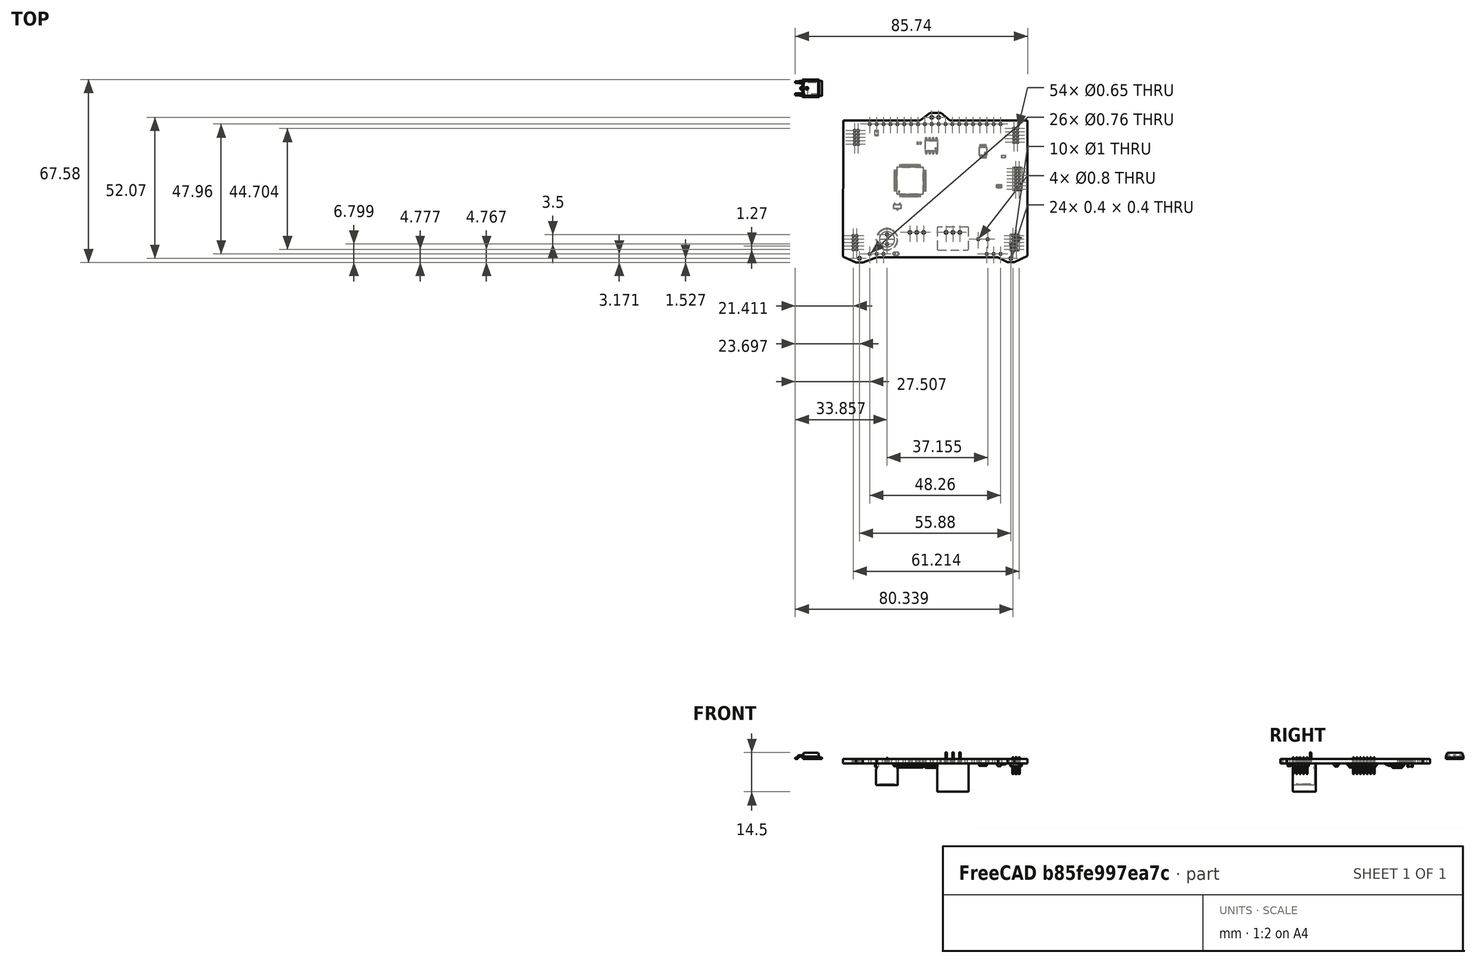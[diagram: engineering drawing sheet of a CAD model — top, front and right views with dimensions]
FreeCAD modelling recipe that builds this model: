
FCSTD DOCUMENT  (FreeCAD 1.0R39109 (Git))
Label: DICMainboard
License: All rights reserved
LicenseURL: http://en.wikipedia.org/wiki/All_rights_reserved
objects: App::Link×97, Part::Feature×24, App::Part×10, PartDesign::CoordinateSystem×1, Sketcher::SketchObject×1
note: 27 computed .brp shape members not serialized (recipe doc carries the construction recipe); baked Part::Feature solids carry a one-line shape summary decoded from their .brp

FEATURE [PartDesign::CoordinateSystem] Local_CS_e9e
  AttacherType = Attacher::AttachEngine3D
  MapMode = 2
FEATURE [Part::Feature] Pcb_e9e
  shape: bbox 68.07 x 55.25 x 1.6 mm, 110 faces (baked)
FEATURE [Sketcher::SketchObject] PCB_Sketch_e9e
  ArcFitTolerance = 1e-06
  FullyConstrained = true
  MakeInternals = false
FEATURE [Part::Feature] Shape  label="C19_C_0805_2012Metric_915db11c73f1"
  Placement = pos=(24.257,-16.448,-1.6) rot=(0.707107,0.707107,0;3.14159rad)
  shape: bbox 1.25 x 2 x 1.25 mm, 28 faces (baked)
FEATURE [Part::Feature] Shape001  label="C18_C_0603_1608Metric_10e447ca614a"
  Placement = pos=(39.878,-20.193,-1.6) rot=(1,0,0;3.14159rad)
  shape: bbox 1.6 x 0.8 x 0.8 mm, 28 faces (baked)
FEATURE [Part::Feature] Shape002  label="R42_R_0603_1608Metric_e00ced120b5b"
  Placement = pos=(70.993,-25.146,-1.6) rot=(1,0,0;3.14159rad)
  shape: bbox 1.6 x 0.8 x 0.45 mm, 26 faces (baked)
FEATURE [App::Link] R42_R_0603_1608Metric_e00ced120b5b_ln_  label="R3_R_0603_1608Metric_9b0ed8f2439a"
  LinkPlacement = pos=(35.687,-42.037,-1.6) rot=(1,0,0;3.14159rad)
  LinkedObject = -> Shape002
  Placement = pos=(35.687,-42.037,-1.6) rot=(1,0,0;3.14159rad)
FEATURE [App::Link] R42_R_0603_1608Metric_e00ced120b5b_ln_001  label="R2_R_0603_1608Metric_8df39385d074"
  LinkPlacement = pos=(27.265,-19.939,-1.6) rot=(0,1,0;3.14159rad)
  LinkedObject = -> Shape002
  Placement = pos=(27.265,-19.939,-1.6) rot=(0,1,0;3.14159rad)
FEATURE [Part::Feature] Shape003  label="C21_CP_Radial_D80mm_P350mm_b4bb79b80bd8"
  Placement = pos=(28.067,-57.531,-1.6) rot=(0.707107,0.707107,0;3.14159rad)
  shape: bbox 10.23 x 9.886 x 10 mm, 54 faces (baked)
FEATURE [App::Link] C19_C_0805_2012Metric_915db11c73f1_ln_  label="C12_C_0805_2012Metric_6993a4fefcef"
  LinkPlacement = pos=(29.972,-40.386,-1.6) rot=(0,1,0;3.14159rad)
  LinkedObject = -> Shape
  Placement = pos=(29.972,-40.386,-1.6) rot=(0,1,0;3.14159rad)
FEATURE [Part::Feature] Shape004  label="JTAG1_PinHeader_2x07_P127mm_Vertical_7ea92a9874db"
  Placement = pos=(76.835,-29.718,-1.6) rot=(0,1,0;3.14159rad)
  shape: bbox 3.4 x 8.89 x 6.3 mm, 298 faces (baked)
FEATURE [App::Link] R42_R_0603_1608Metric_e00ced120b5b_ln_002  label="R29_R_0603_1608Metric_b834401a76b2"
  LinkPlacement = pos=(60.579,-46.228,-1.6) rot=(0,1,0;3.14159rad)
  LinkedObject = -> Shape002
  Placement = pos=(60.579,-46.228,-1.6) rot=(0,1,0;3.14159rad)
FEATURE [App::Link] C18_C_0603_1608Metric_10e447ca614a_ln_  label="C29_C_0603_1608Metric_30aa2c5fb68f"
  LinkPlacement = pos=(50.546,-26.035,-1.6) rot=(1,0,0;3.14159rad)
  LinkedObject = -> Shape001
  Placement = pos=(50.546,-26.035,-1.6) rot=(1,0,0;3.14159rad)
FEATURE [App::Link] R42_R_0603_1608Metric_e00ced120b5b_ln_003  label="R36_R_0603_1608Metric_5693be527eb2"
  LinkPlacement = pos=(53.848,-26.035,-1.6) rot=(0,1,0;3.14159rad)
  LinkedObject = -> Shape002
  Placement = pos=(53.848,-26.035,-1.6) rot=(0,1,0;3.14159rad)
FEATURE [App::Link] R42_R_0603_1608Metric_e00ced120b5b_ln_004  label="R39_R_0603_1608Metric_50952633201f"
  LinkPlacement = pos=(69.215,-29.845,-1.6) rot=(0.707107,0.707107,0;3.14159rad)
  LinkedObject = -> Shape002
  Placement = pos=(69.215,-29.845,-1.6) rot=(0.707107,0.707107,0;3.14159rad)
FEATURE [Part::Feature] Shape005  label="U2_SOT_23_5143090a7d01"
  Placement = pos=(31.877,-43.688,-1.6) rot=(0.707107,-0.707107,0;3.14159rad)
  shape: bbox 3 x 2.5 x 1.2 mm, 76 faces (baked)
FEATURE [App::Link] U2_SOT_23_5143090a7d01_ln_  label="Q2_SOT_23_a46526c7cbaa"
  LinkPlacement = pos=(65.786,-38.735,-1.6) rot=(0.707107,0.707107,0;3.14159rad)
  LinkedObject = -> Shape005
  Placement = pos=(65.786,-38.735,-1.6) rot=(0.707107,0.707107,0;3.14159rad)
FEATURE [App::Link] R42_R_0603_1608Metric_e00ced120b5b_ln_005  label="R31_R_0603_1608Metric_b000aee3d83a"
  LinkPlacement = pos=(59.309,-28.702,-1.6) rot=(0,1,0;3.14159rad)
  LinkedObject = -> Shape002
  Placement = pos=(59.309,-28.702,-1.6) rot=(0,1,0;3.14159rad)
FEATURE [App::Link] C18_C_0603_1608Metric_10e447ca614a_ln_001  label="C5_C_0603_1608Metric_679d8c6e1927"
  LinkPlacement = pos=(34.417,-44.45,-1.6) rot=(0.707107,0.707107,0;3.14159rad)
  LinkedObject = -> Shape001
  Placement = pos=(34.417,-44.45,-1.6) rot=(0.707107,0.707107,0;3.14159rad)
FEATURE [App::Link] C18_C_0603_1608Metric_10e447ca614a_ln_002  label="C6_C_0603_1608Metric_e41e872100cf"
  LinkPlacement = pos=(39.116,-24.322,-1.6) rot=(0,1,0;3.14159rad)
  LinkedObject = -> Shape001
  Placement = pos=(39.116,-24.322,-1.6) rot=(0,1,0;3.14159rad)
FEATURE [Part::Feature] Shape006  label="12VGood1_LED_0805_2012Metric_2ad75f4ca093"
  Placement = pos=(69.469,-36.195,-1.6) rot=(0,1,0;3.14159rad)
  shape: bbox 2 x 1.25 x 1.1 mm, 50 faces (baked)
FEATURE [App::Link] C19_C_0805_2012Metric_915db11c73f1_ln_001  label="C14_C_0805_2012Metric_060f63ed2ef4"
  LinkPlacement = pos=(42.418,-49.911,-1.6) rot=(1,0,0;3.14159rad)
  LinkedObject = -> Shape
  Placement = pos=(42.418,-49.911,-1.6) rot=(1,0,0;3.14159rad)
FEATURE [App::Link] R42_R_0603_1608Metric_e00ced120b5b_ln_006  label="R30_R_0603_1608Metric_8c3fd63a3134"
  LinkPlacement = pos=(50.8,-42.926,-1.6) rot=(0,1,0;3.14159rad)
  LinkedObject = -> Shape002
  Placement = pos=(50.8,-42.926,-1.6) rot=(0,1,0;3.14159rad)
FEATURE [App::Link] C18_C_0603_1608Metric_10e447ca614a_ln_003  label="C17_C_0603_1608Metric_5bd1929c3623"
  LinkPlacement = pos=(39.878,-21.971,-1.6) rot=(1,0,0;3.14159rad)
  LinkedObject = -> Shape001
  Placement = pos=(39.878,-21.971,-1.6) rot=(1,0,0;3.14159rad)
FEATURE [App::Link] R42_R_0603_1608Metric_e00ced120b5b_ln_007  label="R25_R_0603_1608Metric_14260ea3fd4e"
  LinkPlacement = pos=(64.77,-44.704,-1.6) rot=(0,1,0;3.14159rad)
  LinkedObject = -> Shape002
  Placement = pos=(64.77,-44.704,-1.6) rot=(0,1,0;3.14159rad)
FEATURE [Part::Feature] Shape007  label="U10_MSOP_8_3x3mm_P065mm_82bb67e16242"
  Placement = pos=(63.5,-23.241,-1.6) rot=(0.707107,0.707107,0;3.14159rad)
  shape: bbox 3 x 4.9 x 0.95 mm, 156 faces (baked)
FEATURE [App::Link] U2_SOT_23_5143090a7d01_ln_001  label="Q1_SOT_23_1223d9ad7d7e"
  LinkPlacement = pos=(68.072,-33.274,-1.6) rot=(1,0,0;3.14159rad)
  LinkedObject = -> Shape005
  Placement = pos=(68.072,-33.274,-1.6) rot=(1,0,0;3.14159rad)
FEATURE [App::Link] C19_C_0805_2012Metric_915db11c73f1_ln_002  label="C11_C_0805_2012Metric_20aa78c893d6"
  LinkPlacement = pos=(54.2075,-49.53,-1.6) rot=(0,1,0;3.14159rad)
  LinkedObject = -> Shape
  Placement = pos=(54.2075,-49.53,-1.6) rot=(0,1,0;3.14159rad)
FEATURE [Part::Feature] Shape008  label="J3_PinHeader_2x05_P127mm_Vertical_4a0e541a8516"
  Placement = pos=(75.819,-54.473,-1.6) rot=(0,1,0;3.14159rad)
  shape: bbox 3.4 x 6.35 x 6.3 mm, 214 faces (baked)
FEATURE [App::Link] R42_R_0603_1608Metric_e00ced120b5b_ln_008  label="R1_R_0603_1608Metric_52185c8e4965"
  LinkPlacement = pos=(27.265,-22.733,-1.6) rot=(1,0,0;3.14159rad)
  LinkedObject = -> Shape002
  Placement = pos=(27.265,-22.733,-1.6) rot=(1,0,0;3.14159rad)
FEATURE [App::Link] C19_C_0805_2012Metric_915db11c73f1_ln_003  label="C7_C_0805_2012Metric_b3b50e9b0364"
  LinkPlacement = pos=(50.2705,-49.53,-1.6) rot=(1,0,0;3.14159rad)
  LinkedObject = -> Shape
  Placement = pos=(50.2705,-49.53,-1.6) rot=(1,0,0;3.14159rad)
FEATURE [App::Link] U10_MSOP_8_3x3mm_P065mm_82bb67e16242_ln_  label="U9_MSOP_8_3x3mm_P065mm_9b50181ec5fb"
  LinkPlacement = pos=(57.023,-41.91,-1.6) rot=(1,0,0;3.14159rad)
  LinkedObject = -> Shape007
  Placement = pos=(57.023,-41.91,-1.6) rot=(1,0,0;3.14159rad)
FEATURE [App::Link] _2VGood1_LED_0805_2012Metric_2ad75f4ca093_ln_  label="5VGood1_LED_0805_2012Metric_60cda601a8c1"
  LinkPlacement = pos=(51.943,-60.96,-1.6) rot=(0,1,0;3.14159rad)
  LinkedObject = -> Shape006
  Placement = pos=(51.943,-60.96,-1.6) rot=(0,1,0;3.14159rad)
FEATURE [App::Link] U2_SOT_23_5143090a7d01_ln_002  label="Q3_SOT_23_1241f12d323f"
  LinkPlacement = pos=(59.055,-32.766,-1.6) rot=(1,0,0;3.14159rad)
  LinkedObject = -> Shape005
  Placement = pos=(59.055,-32.766,-1.6) rot=(1,0,0;3.14159rad)
FEATURE [App::Link] C18_C_0603_1608Metric_10e447ca614a_ln_004  label="C2_C_0603_1608Metric_784de1c4b5be"
  LinkPlacement = pos=(27.178,-37.28,-1.6) rot=(0.707107,0.707107,0;3.14159rad)
  LinkedObject = -> Shape001
  Placement = pos=(27.178,-37.28,-1.6) rot=(0.707107,0.707107,0;3.14159rad)
FEATURE [Part::Feature] Shape009  label="D10_D_SOD_323_1cf1e5386782"
  Placement = pos=(31.369,-61.087,-1.6) rot=(1,0,0;3.14159rad)
  shape: bbox 2.5 x 1.25 x 1.1 mm, 67 faces (baked)
FEATURE [App::Link] D10_D_SOD_323_1cf1e5386782_ln_  label="D8_D_SOD_323_442fc4d99dd7"
  LinkPlacement = pos=(52.324,-24.257,-1.6) rot=(1,0,0;3.14159rad)
  LinkedObject = -> Shape009
  Placement = pos=(52.324,-24.257,-1.6) rot=(1,0,0;3.14159rad)
FEATURE [App::Link] R42_R_0603_1608Metric_e00ced120b5b_ln_009  label="R46_R_0603_1608Metric_d391e1cc1bf8"
  LinkPlacement = pos=(55.88,-18.923,-1.6) rot=(1,0,0;3.14159rad)
  LinkedObject = -> Shape002
  Placement = pos=(55.88,-18.923,-1.6) rot=(1,0,0;3.14159rad)
FEATURE [App::Link] R42_R_0603_1608Metric_e00ced120b5b_ln_010  label="R44_R_0603_1608Metric_76086e2af044"
  LinkPlacement = pos=(70.993,-21.59,-1.6) rot=(0,1,0;3.14159rad)
  LinkedObject = -> Shape002
  Placement = pos=(70.993,-21.59,-1.6) rot=(0,1,0;3.14159rad)
FEATURE [App::Link] R42_R_0603_1608Metric_e00ced120b5b_ln_011  label="R24_R_0603_1608Metric_616434719463"
  LinkPlacement = pos=(62.357,-43.815,-1.6) rot=(0.707107,-0.707107,0;3.14159rad)
  LinkedObject = -> Shape002
  Placement = pos=(62.357,-43.815,-1.6) rot=(0.707107,-0.707107,0;3.14159rad)
FEATURE [App::Link] U2_SOT_23_5143090a7d01_ln_003  label="Q6_SOT_23_f7e973546728"
  LinkPlacement = pos=(67.31,-23.876,-1.6) rot=(1,0,0;3.14159rad)
  LinkedObject = -> Shape005
  Placement = pos=(67.31,-23.876,-1.6) rot=(1,0,0;3.14159rad)
FEATURE [App::Link] C18_C_0603_1608Metric_10e447ca614a_ln_005  label="C31_C_0603_1608Metric_179902ffe984"
  LinkPlacement = pos=(58.801,-24.638,-1.6) rot=(1,0,0;3.14159rad)
  LinkedObject = -> Shape001
  Placement = pos=(58.801,-24.638,-1.6) rot=(1,0,0;3.14159rad)
FEATURE [App::Link] C18_C_0603_1608Metric_10e447ca614a_ln_006  label="C25_C_0603_1608Metric_a51b3fc9b87c"
  LinkPlacement = pos=(48.26,-46.101,-1.6) rot=(1,0,0;3.14159rad)
  LinkedObject = -> Shape001
  Placement = pos=(48.26,-46.101,-1.6) rot=(1,0,0;3.14159rad)
FEATURE [App::Link] J3_PinHeader_2x05_P127mm_Vertical_4a0e541a8516_ln_  label="J5_PinHeader_2x05_P127mm_Vertical_21cfdfc90ae7"
  LinkPlacement = pos=(16.891,-54.483,-1.6) rot=(0,1,0;3.14159rad)
  LinkedObject = -> Shape008
  Placement = pos=(16.891,-54.483,-1.6) rot=(0,1,0;3.14159rad)
FEATURE [App::Link] D10_D_SOD_323_1cf1e5386782_ln_001  label="D2_D_SOD_323_81fae5dc7b6e"
  LinkPlacement = pos=(47.371,-48.895,-1.6) rot=(0.707107,0.707107,0;3.14159rad)
  LinkedObject = -> Shape009
  Placement = pos=(47.371,-48.895,-1.6) rot=(0.707107,0.707107,0;3.14159rad)
FEATURE [App::Link] R42_R_0603_1608Metric_e00ced120b5b_ln_012  label="R28_R_0603_1608Metric_524fb33c0c76"
  LinkPlacement = pos=(59.7385,-49.596,-1.6) rot=(0.707107,0.707107,0;3.14159rad)
  LinkedObject = -> Shape002
  Placement = pos=(59.7385,-49.596,-1.6) rot=(0.707107,0.707107,0;3.14159rad)
FEATURE [App::Link] R42_R_0603_1608Metric_e00ced120b5b_ln_013  label="R9_R_0603_1608Metric_39820daff148"
  LinkPlacement = pos=(31.877,-18.607,-1.6) rot=(0.707107,0.707107,0;3.14159rad)
  LinkedObject = -> Shape002
  Placement = pos=(31.877,-18.607,-1.6) rot=(0.707107,0.707107,0;3.14159rad)
FEATURE [App::Link] C18_C_0603_1608Metric_10e447ca614a_ln_007  label="C28_C_0603_1608Metric_9930d46ac3f8"
  LinkPlacement = pos=(53.467,-18.288,-1.6) rot=(0.707107,0.707107,0;3.14159rad)
  LinkedObject = -> Shape001
  Placement = pos=(53.467,-18.288,-1.6) rot=(0.707107,0.707107,0;3.14159rad)
FEATURE [App::Link] R42_R_0603_1608Metric_e00ced120b5b_ln_014  label="R23_R_0603_1608Metric_14708d2771e9"
  LinkPlacement = pos=(68.199,-51.308,-1.6) rot=(0.707107,-0.707107,0;3.14159rad)
  LinkedObject = -> Shape002
  Placement = pos=(68.199,-51.308,-1.6) rot=(0.707107,-0.707107,0;3.14159rad)
FEATURE [App::Link] C19_C_0805_2012Metric_915db11c73f1_ln_004  label="C23_C_0805_2012Metric_29fb196ac7a2"
  LinkPlacement = pos=(70.231,-40.386,-1.6) rot=(0,1,0;3.14159rad)
  LinkedObject = -> Shape
  Placement = pos=(70.231,-40.386,-1.6) rot=(0,1,0;3.14159rad)
FEATURE [Part::Feature] Shape010  label="U1_Converter_DCDC_RECOM_R_78E_05_THT_7495ffbcc0e0"
  Placement = pos=(49.877,-53.213,-1.6) rot=(1,0,0;3.14159rad)
  shape: bbox 11.67 x 8.57 x 14.5 mm, 27 faces (baked)
FEATURE [App::Link] _2VGood1_LED_0805_2012Metric_2ad75f4ca093_ln_001  label="Error1_LED_0805_2012Metric_0193bb44fb5e"
  LinkPlacement = pos=(23.455,-19.939,-1.6) rot=(0,1,0;3.14159rad)
  LinkedObject = -> Shape006
  Placement = pos=(23.455,-19.939,-1.6) rot=(0,1,0;3.14159rad)
FEATURE [App::Link] C19_C_0805_2012Metric_915db11c73f1_ln_005  label="C15_C_0805_2012Metric_c2950c4f82bb"
  LinkPlacement = pos=(45.339,-49.022,-1.6) rot=(0.707107,0.707107,0;3.14159rad)
  LinkedObject = -> Shape
  Placement = pos=(45.339,-49.022,-1.6) rot=(0.707107,0.707107,0;3.14159rad)
FEATURE [App::Link] R42_R_0603_1608Metric_e00ced120b5b_ln_015  label="R11_R_0603_1608Metric_fc6ec5a46fb0"
  LinkPlacement = pos=(44.45,-16.699,-1.6) rot=(1,0,0;3.14159rad)
  LinkedObject = -> Shape002
  Placement = pos=(44.45,-16.699,-1.6) rot=(1,0,0;3.14159rad)
FEATURE [App::Link] R42_R_0603_1608Metric_e00ced120b5b_ln_016  label="R43_R_0603_1608Metric_bffcf2708168"
  LinkPlacement = pos=(65.786,-17.907,-1.6) rot=(0,1,0;3.14159rad)
  LinkedObject = -> Shape002
  Placement = pos=(65.786,-17.907,-1.6) rot=(0,1,0;3.14159rad)
FEATURE [App::Link] D10_D_SOD_323_1cf1e5386782_ln_002  label="D3_D_SOD_323_b8dc3af82ad9"
  LinkPlacement = pos=(58.674,-22.225,-1.6) rot=(1,0,0;3.14159rad)
  LinkedObject = -> Shape009
  Placement = pos=(58.674,-22.225,-1.6) rot=(1,0,0;3.14159rad)
FEATURE [App::Link] R42_R_0603_1608Metric_e00ced120b5b_ln_017  label="R38_R_0603_1608Metric_037dd372ccbc"
  LinkPlacement = pos=(70.739,-27.686,-1.6) rot=(0.707107,0.707107,0;3.14159rad)
  LinkedObject = -> Shape002
  Placement = pos=(70.739,-27.686,-1.6) rot=(0.707107,0.707107,0;3.14159rad)
FEATURE [App::Link] C19_C_0805_2012Metric_915db11c73f1_ln_006  label="C20_C_0805_2012Metric_feb99ca7776e"
  LinkPlacement = pos=(31.877,-15.686,-1.6) rot=(0,1,0;3.14159rad)
  LinkedObject = -> Shape
  Placement = pos=(31.877,-15.686,-1.6) rot=(0,1,0;3.14159rad)
FEATURE [App::Link] R42_R_0603_1608Metric_e00ced120b5b_ln_018  label="R37_R_0603_1608Metric_1e3016d2806e"
  LinkPlacement = pos=(70.993,-23.241,-1.6) rot=(0,1,0;3.14159rad)
  LinkedObject = -> Shape002
  Placement = pos=(70.993,-23.241,-1.6) rot=(0,1,0;3.14159rad)
FEATURE [Part::Feature] Shape011  label="U7_SOIC_8_39x49mm_P127mm_1499a48e6e93"
  Placement = pos=(44.45,-21.209,-1.6) rot=(0.707107,0.707107,0;3.14159rad)
  shape: bbox 4.9 x 6 x 1.75 mm, 156 faces (baked)
FEATURE [App::Link] R42_R_0603_1608Metric_e00ced120b5b_ln_019  label="R10_R_0603_1608Metric_863b16e2652c"
  LinkPlacement = pos=(48.133,-19.558,-1.6) rot=(0.707107,0.707107,0;3.14159rad)
  LinkedObject = -> Shape002
  Placement = pos=(48.133,-19.558,-1.6) rot=(0.707107,0.707107,0;3.14159rad)
FEATURE [App::Link] R42_R_0603_1608Metric_e00ced120b5b_ln_020  label="R7_R_0603_1608Metric_1723f24f5f2f"
  LinkPlacement = pos=(78.105,-43.688,-1.6) rot=(0.707107,0.707107,0;3.14159rad)
  LinkedObject = -> Shape002
  Placement = pos=(78.105,-43.688,-1.6) rot=(0.707107,0.707107,0;3.14159rad)
FEATURE [App::Link] C18_C_0603_1608Metric_10e447ca614a_ln_008  label="C4_C_0603_1608Metric_5f5500ef63df"
  LinkPlacement = pos=(32.131,-25.146,-1.6) rot=(0,1,0;3.14159rad)
  LinkedObject = -> Shape001
  Placement = pos=(32.131,-25.146,-1.6) rot=(0,1,0;3.14159rad)
FEATURE [App::Link] R42_R_0603_1608Metric_e00ced120b5b_ln_021  label="R17_R_0603_1608Metric_fc738fbfad18"
  LinkPlacement = pos=(70.739,-30.988,-1.6) rot=(0.707107,0.707107,0;3.14159rad)
  LinkedObject = -> Shape002
  Placement = pos=(70.739,-30.988,-1.6) rot=(0.707107,0.707107,0;3.14159rad)
FEATURE [App::Link] U2_SOT_23_5143090a7d01_ln_004  label="Q7_SOT_23_bc60db84acee"
  LinkPlacement = pos=(63.627,-29.845,-1.6) rot=(1,0,0;3.14159rad)
  LinkedObject = -> Shape005
  Placement = pos=(63.627,-29.845,-1.6) rot=(1,0,0;3.14159rad)
FEATURE [App::Link] U1_Converter_DCDC_RECOM_R_78E_05_THT_7495ffbcc0e0_ln_  label="U5_Converter_DCDC_RECOM_R_78E_05_THT_6eb4cbfbcd04"
  LinkPlacement = pos=(36.542,-53.213,-1.6) rot=(1,0,0;3.14159rad)
  LinkedObject = -> Shape010
  Placement = pos=(36.542,-53.213,-1.6) rot=(1,0,0;3.14159rad)
FEATURE [App::Link] R42_R_0603_1608Metric_e00ced120b5b_ln_022  label="R26_R_0603_1608Metric_34ca61038909"
  LinkPlacement = pos=(67.691,-28.829,-1.6) rot=(0.707107,-0.707107,0;3.14159rad)
  LinkedObject = -> Shape002
  Placement = pos=(67.691,-28.829,-1.6) rot=(0.707107,-0.707107,0;3.14159rad)
FEATURE [App::Link] R42_R_0603_1608Metric_e00ced120b5b_ln_023  label="R27_R_0603_1608Metric_60e756865c77"
  LinkPlacement = pos=(67.183,-43.815,-1.6) rot=(0.707107,0.707107,0;3.14159rad)
  LinkedObject = -> Shape002
  Placement = pos=(67.183,-43.815,-1.6) rot=(0.707107,0.707107,0;3.14159rad)
FEATURE [App::Link] R42_R_0603_1608Metric_e00ced120b5b_ln_024  label="R14_R_0603_1608Metric_d767aa6e1c7e"
  LinkPlacement = pos=(58.928,-37.592,-1.6) rot=(0,1,0;3.14159rad)
  LinkedObject = -> Shape002
  Placement = pos=(58.928,-37.592,-1.6) rot=(0,1,0;3.14159rad)
FEATURE [App::Link] R42_R_0603_1608Metric_e00ced120b5b_ln_025  label="R35_R_0603_1608Metric_a89be60451e6"
  LinkPlacement = pos=(67.056,-26.416,-1.6) rot=(0,1,0;3.14159rad)
  LinkedObject = -> Shape002
  Placement = pos=(67.056,-26.416,-1.6) rot=(0,1,0;3.14159rad)
FEATURE [App::Link] R42_R_0603_1608Metric_e00ced120b5b_ln_026  label="R12_R_0603_1608Metric_98ba704dd8f1"
  LinkPlacement = pos=(65.786,-41.402,-1.6) rot=(0,1,0;3.14159rad)
  LinkedObject = -> Shape002
  Placement = pos=(65.786,-41.402,-1.6) rot=(0,1,0;3.14159rad)
FEATURE [App::Link] C18_C_0603_1608Metric_10e447ca614a_ln_009  label="C1_C_0603_1608Metric_84c5a7f979f1"
  LinkPlacement = pos=(32.131,-23.495,-1.6) rot=(0,1,0;3.14159rad)
  LinkedObject = -> Shape001
  Placement = pos=(32.131,-23.495,-1.6) rot=(0,1,0;3.14159rad)
FEATURE [App::Link] U2_SOT_23_5143090a7d01_ln_005  label="Q5_SOT_23_2fb3d1e9febb"
  LinkPlacement = pos=(62.9135,-49.596,-1.6) rot=(1,0,0;3.14159rad)
  LinkedObject = -> Shape005
  Placement = pos=(62.9135,-49.596,-1.6) rot=(1,0,0;3.14159rad)
FEATURE [App::Link] _2VGood1_LED_0805_2012Metric_2ad75f4ca093_ln_002  label="Heart1_LED_0805_2012Metric_c9bdaa238e08"
  LinkPlacement = pos=(23.455,-22.733,-1.6) rot=(0,1,0;3.14159rad)
  LinkedObject = -> Shape006
  Placement = pos=(23.455,-22.733,-1.6) rot=(0,1,0;3.14159rad)
FEATURE [App::Link] C18_C_0603_1608Metric_10e447ca614a_ln_010  label="C8_C_0603_1608Metric_bdc2e3e24877"
  LinkPlacement = pos=(39.116,-25.973,-1.6) rot=(0,1,0;3.14159rad)
  LinkedObject = -> Shape001
  Placement = pos=(39.116,-25.973,-1.6) rot=(0,1,0;3.14159rad)
FEATURE [App::Link] C19_C_0805_2012Metric_915db11c73f1_ln_007  label="C22_C_0805_2012Metric_28f6afd9b51f"
  LinkPlacement = pos=(69.977,-54.61,-1.6) rot=(0,1,0;3.14159rad)
  LinkedObject = -> Shape
  Placement = pos=(69.977,-54.61,-1.6) rot=(0,1,0;3.14159rad)
FEATURE [App::Link] C18_C_0603_1608Metric_10e447ca614a_ln_011  label="C3_C_0603_1608Metric_22f7aa9a1690"
  LinkPlacement = pos=(27.178,-33.782,-1.6) rot=(0.707107,-0.707107,0;3.14159rad)
  LinkedObject = -> Shape001
  Placement = pos=(27.178,-33.782,-1.6) rot=(0.707107,-0.707107,0;3.14159rad)
FEATURE [App::Link] R42_R_0603_1608Metric_e00ced120b5b_ln_027  label="R20_R_0603_1608Metric_2b4dd9f72b59"
  LinkPlacement = pos=(57.404,-39.116,-1.6) rot=(1,0,0;3.14159rad)
  LinkedObject = -> Shape002
  Placement = pos=(57.404,-39.116,-1.6) rot=(1,0,0;3.14159rad)
FEATURE [App::Link] R42_R_0603_1608Metric_e00ced120b5b_ln_028  label="R8_R_0603_1608Metric_7230250cfa97"
  LinkPlacement = pos=(69.596,-38.354,-1.6) rot=(1,0,0;3.14159rad)
  LinkedObject = -> Shape002
  Placement = pos=(69.596,-38.354,-1.6) rot=(1,0,0;3.14159rad)
FEATURE [App::Link] R42_R_0603_1608Metric_e00ced120b5b_ln_029  label="R6_R_0603_1608Metric_956f91f139f8"
  LinkPlacement = pos=(43.434,-60.96,-1.6) rot=(1,0,0;3.14159rad)
  LinkedObject = -> Shape002
  Placement = pos=(43.434,-60.96,-1.6) rot=(1,0,0;3.14159rad)
FEATURE [App::Link] R42_R_0603_1608Metric_e00ced120b5b_ln_030  label="R15_R_0603_1608Metric_29f9765fedca"
  LinkPlacement = pos=(57.15,-36.068,-1.6) rot=(0,1,0;3.14159rad)
  LinkedObject = -> Shape002
  Placement = pos=(57.15,-36.068,-1.6) rot=(0,1,0;3.14159rad)
FEATURE [App::Link] _2VGood1_LED_0805_2012Metric_2ad75f4ca093_ln_003  label="3V3Good1_LED_0805_2012Metric_f770177cd55f"
  LinkPlacement = pos=(39.624,-60.96,-1.6) rot=(1,0,0;3.14159rad)
  LinkedObject = -> Shape006
  Placement = pos=(39.624,-60.96,-1.6) rot=(1,0,0;3.14159rad)
FEATURE [App::Link] R42_R_0603_1608Metric_e00ced120b5b_ln_031  label="R13_R_0603_1608Metric_88249867bc70"
  LinkPlacement = pos=(64.389,-33.528,-1.6) rot=(0,1,0;3.14159rad)
  LinkedObject = -> Shape002
  Placement = pos=(64.389,-33.528,-1.6) rot=(0,1,0;3.14159rad)
FEATURE [App::Link] R42_R_0603_1608Metric_e00ced120b5b_ln_032  label="R18_R_0603_1608Metric_e7deeba773bd"
  LinkPlacement = pos=(54.991,-33.655,-1.6) rot=(0,1,0;3.14159rad)
  LinkedObject = -> Shape002
  Placement = pos=(54.991,-33.655,-1.6) rot=(0,1,0;3.14159rad)
FEATURE [App::Link] R42_R_0603_1608Metric_e00ced120b5b_ln_033  label="R41_R_0603_1608Metric_2dfa8f3c3e90"
  LinkPlacement = pos=(59.436,-18.796,-1.6) rot=(0.707107,-0.707107,0;3.14159rad)
  LinkedObject = -> Shape002
  Placement = pos=(59.436,-18.796,-1.6) rot=(0.707107,-0.707107,0;3.14159rad)
FEATURE [App::Link] C18_C_0603_1608Metric_10e447ca614a_ln_012  label="C30_C_0603_1608Metric_0742e3473aaa"
  LinkPlacement = pos=(50.8,-41.402,-1.6) rot=(0,1,0;3.14159rad)
  LinkedObject = -> Shape001
  Placement = pos=(50.8,-41.402,-1.6) rot=(0,1,0;3.14159rad)
FEATURE [App::Link] R42_R_0603_1608Metric_e00ced120b5b_ln_034  label="R21_R_0603_1608Metric_9688ea295803"
  LinkPlacement = pos=(51.308,-36.957,-1.6) rot=(1,0,0;3.14159rad)
  LinkedObject = -> Shape002
  Placement = pos=(51.308,-36.957,-1.6) rot=(1,0,0;3.14159rad)
FEATURE [App::Link] J3_PinHeader_2x05_P127mm_Vertical_4a0e541a8516_ln_001  label="J4_PinHeader_2x05_P127mm_Vertical_89510c161731"
  LinkPlacement = pos=(16.129,-20.701,-1.6) rot=(1,0,0;3.14159rad)
  LinkedObject = -> Shape008
  Placement = pos=(16.129,-20.701,-1.6) rot=(1,0,0;3.14159rad)
FEATURE [Part::Feature] Part__Feature  label="932d09b3-9c39-11ed-93f0-dde97e994e83_part"
  shape: bbox 6.22 x 6.5 x 2.3 mm, 13 faces (baked)
FEATURE [App::Part] _32d09b3_9c39_11ed_93f0_dde97e994e83  label="932d09b3-9c39-11ed-93f0-dde97e994e83"
  Group = -> [Part__Feature]
  Origin = -> Origin008
FEATURE [Part::Feature] Part__Feature001  label="932d09b4-9c39-11ed-93f0-dde97e994e83_part"
  shape: bbox 5.24 x 5.4 x 0.5 mm, 16 faces (baked)
FEATURE [App::Part] _32d09b4_9c39_11ed_93f0_dde97e994e83  label="932d09b4-9c39-11ed-93f0-dde97e994e83"
  Group = -> [Part__Feature001]
  Origin = -> Origin009
FEATURE [Part::Feature] Part__Feature002  label="932d09b5-9c39-11ed-93f0-dde97e994e83_part"
  shape: bbox 3.552 x 0.99 x 1.44 mm, 22 faces (baked)
FEATURE [Part::Feature] Part__Feature003  label="932d09b5-9c39-11ed-93f0-dde97e994e83_part001"
  shape: bbox 1.672 x 0.99 x 0.5 mm, 10 faces (baked)
FEATURE [Part::Feature] Part__Feature004  label="932d09b5-9c39-11ed-93f0-dde97e994e83_part002"
  shape: bbox 3.552 x 0.99 x 1.44 mm, 22 faces (baked)
FEATURE [App::Part] _32d09b5_9c39_11ed_93f0_dde97e994e83_part  label="932d09b5-9c39-11ed-93f0-dde97e994e83_part003"
  Group = -> [Part__Feature002,Part__Feature003,Part__Feature004]
  Origin = -> Origin010
FEATURE [App::Part] _32d09b5_9c39_11ed_93f0_dde97e994e83  label="932d09b5-9c39-11ed-93f0-dde97e994e83"
  Group = -> [_32d09b5_9c39_11ed_93f0_dde97e994e83_part]
  Origin = -> Origin011
FEATURE [App::Part] _32d09b2_9c39_11ed_93f0_dde97e994e83  label="932d09b2-9c39-11ed-93f0-dde97e994e83"
  Group = -> [_32d09b3_9c39_11ed_93f0_dde97e994e83,_32d09b4_9c39_11ed_93f0_dde97e994e83,_32d09b5_9c39_11ed_93f0_dde97e994e83]
  Origin = -> Origin012
FEATURE [App::Part] CQ_assembly  label="U8_CQ assembly_9e30a5f4f37c"
  Group = -> [_32d09b2_9c39_11ed_93f0_dde97e994e83]
  Origin = -> Origin013
  Placement = pos=(73.025,-46.472,-1.6) rot=(0.707107,0.707107,0;3.14159rad)
FEATURE [App::Link] C19_C_0805_2012Metric_915db11c73f1_ln_008  label="C26_C_0805_2012Metric_58a7a7612ec2"
  LinkPlacement = pos=(57.15,-47.244,-1.6) rot=(0.707107,-0.707107,0;3.14159rad)
  LinkedObject = -> Shape
  Placement = pos=(57.15,-47.244,-1.6) rot=(0.707107,-0.707107,0;3.14159rad)
FEATURE [App::Link] R42_R_0603_1608Metric_e00ced120b5b_ln_035  label="R19_R_0603_1608Metric_4285ec9b66e1"
  LinkPlacement = pos=(54.483,-36.957,-1.6) rot=(0.707107,-0.707107,0;3.14159rad)
  LinkedObject = -> Shape002
  Placement = pos=(54.483,-36.957,-1.6) rot=(0.707107,-0.707107,0;3.14159rad)
FEATURE [App::Link] U2_SOT_23_5143090a7d01_ln_006  label="Q8_SOT_23_4a5958cf5442"
  LinkPlacement = pos=(69.85,-17.526,-1.6) rot=(1,0,0;3.14159rad)
  LinkedObject = -> Shape005
  Placement = pos=(69.85,-17.526,-1.6) rot=(1,0,0;3.14159rad)
FEATURE [App::Link] R42_R_0603_1608Metric_e00ced120b5b_ln_036  label="R33_R_0603_1608Metric_c9c509e34e71"
  LinkPlacement = pos=(49.149,-44.577,-1.6) rot=(0,1,0;3.14159rad)
  LinkedObject = -> Shape002
  Placement = pos=(49.149,-44.577,-1.6) rot=(0,1,0;3.14159rad)
FEATURE [App::Link] R42_R_0603_1608Metric_e00ced120b5b_ln_037  label="R34_R_0603_1608Metric_85fe14c106d9"
  LinkPlacement = pos=(53.848,-27.686,-1.6) rot=(1,0,0;3.14159rad)
  LinkedObject = -> Shape002
  Placement = pos=(53.848,-27.686,-1.6) rot=(1,0,0;3.14159rad)
FEATURE [App::Link] R42_R_0603_1608Metric_e00ced120b5b_ln_038  label="R16_R_0603_1608Metric_68531f109549"
  LinkPlacement = pos=(62.357,-37.592,-1.6) rot=(0,1,0;3.14159rad)
  LinkedObject = -> Shape002
  Placement = pos=(62.357,-37.592,-1.6) rot=(0,1,0;3.14159rad)
FEATURE [App::Link] U2_SOT_23_5143090a7d01_ln_007  label="Q4_SOT_23_94e1ef1df5d7"
  LinkPlacement = pos=(67.183,-47.625,-1.6) rot=(0.707107,0.707107,0;3.14159rad)
  LinkedObject = -> Shape005
  Placement = pos=(67.183,-47.625,-1.6) rot=(0.707107,0.707107,0;3.14159rad)
FEATURE [App::Link] D10_D_SOD_323_1cf1e5386782_ln_003  label="D5_D_SOD_323_d6054b8cd4c7"
  LinkPlacement = pos=(49.911,-19.558,-1.6) rot=(0.707107,-0.707107,0;3.14159rad)
  LinkedObject = -> Shape009
  Placement = pos=(49.911,-19.558,-1.6) rot=(0.707107,-0.707107,0;3.14159rad)
FEATURE [App::Link] D10_D_SOD_323_1cf1e5386782_ln_004  label="D4_D_SOD_323_bdc2fbd66cdd"
  LinkPlacement = pos=(53.848,-15.24,-1.6) rot=(1,0,0;3.14159rad)
  LinkedObject = -> Shape009
  Placement = pos=(53.848,-15.24,-1.6) rot=(1,0,0;3.14159rad)
FEATURE [App::Link] C18_C_0603_1608Metric_10e447ca614a_ln_013  label="C10_C_0603_1608Metric_49a17912874c"
  LinkPlacement = pos=(41.529,-41.148,-1.6) rot=(0.707107,-0.707107,0;3.14159rad)
  LinkedObject = -> Shape001
  Placement = pos=(41.529,-41.148,-1.6) rot=(0.707107,-0.707107,0;3.14159rad)
FEATURE [App::Link] C18_C_0603_1608Metric_10e447ca614a_ln_014  label="C9_C_0603_1608Metric_ad1383201845"
  LinkPlacement = pos=(43.053,-40.132,-1.6) rot=(0.707107,-0.707107,0;3.14159rad)
  LinkedObject = -> Shape001
  Placement = pos=(43.053,-40.132,-1.6) rot=(0.707107,-0.707107,0;3.14159rad)
FEATURE [App::Link] R42_R_0603_1608Metric_e00ced120b5b_ln_039  label="R40_R_0603_1608Metric_03e1db1fd9d4"
  LinkPlacement = pos=(62.865,-27.178,-1.6) rot=(0,1,0;3.14159rad)
  LinkedObject = -> Shape002
  Placement = pos=(62.865,-27.178,-1.6) rot=(0,1,0;3.14159rad)
FEATURE [App::Link] D10_D_SOD_323_1cf1e5386782_ln_005  label="D1_D_SOD_323_7cfbc3cf6d88"
  LinkPlacement = pos=(52.197,-32.512,-1.6) rot=(0.707107,-0.707107,0;3.14159rad)
  LinkedObject = -> Shape009
  Placement = pos=(52.197,-32.512,-1.6) rot=(0.707107,-0.707107,0;3.14159rad)
FEATURE [App::Link] R42_R_0603_1608Metric_e00ced120b5b_ln_040  label="R32_R_0603_1608Metric_638f9ad5d960"
  LinkPlacement = pos=(51.816,-45.72,-1.6) rot=(0.707107,0.707107,0;3.14159rad)
  LinkedObject = -> Shape002
  Placement = pos=(51.816,-45.72,-1.6) rot=(0.707107,0.707107,0;3.14159rad)
FEATURE [App::Link] R42_R_0603_1608Metric_e00ced120b5b_ln_041  label="R5_R_0603_1608Metric_eab0520c1254"
  LinkPlacement = pos=(77.343,-46.99,-1.6) rot=(0.707107,-0.707107,0;3.14159rad)
  LinkedObject = -> Shape002
  Placement = pos=(77.343,-46.99,-1.6) rot=(0.707107,-0.707107,0;3.14159rad)
FEATURE [App::Link] R42_R_0603_1608Metric_e00ced120b5b_ln_042  label="R4_R_0603_1608Metric_1c33adfa3623"
  LinkPlacement = pos=(48.133,-60.96,-1.6) rot=(0,1,0;3.14159rad)
  LinkedObject = -> Shape002
  Placement = pos=(48.133,-60.96,-1.6) rot=(0,1,0;3.14159rad)
FEATURE [App::Link] C18_C_0603_1608Metric_10e447ca614a_ln_015  label="C16_C_0603_1608Metric_fd54e4cc6448"
  LinkPlacement = pos=(60.833,-14.986,-1.6) rot=(0,1,0;3.14159rad)
  LinkedObject = -> Shape001
  Placement = pos=(60.833,-14.986,-1.6) rot=(0,1,0;3.14159rad)
FEATURE [App::Link] J3_PinHeader_2x05_P127mm_Vertical_4a0e541a8516_ln_002  label="J2_PinHeader_2x05_P127mm_Vertical_e771ec2928c9"
  LinkPlacement = pos=(76.2,-14.859,-1.6) rot=(0,1,0;3.14159rad)
  LinkedObject = -> Shape008
  Placement = pos=(76.2,-14.859,-1.6) rot=(0,1,0;3.14159rad)
FEATURE [App::Link] C19_C_0805_2012Metric_915db11c73f1_ln_009  label="C27_C_0805_2012Metric_632f8fc273e4"
  LinkPlacement = pos=(55.372,-23.368,-1.6) rot=(0.707107,-0.707107,0;3.14159rad)
  LinkedObject = -> Shape
  Placement = pos=(55.372,-23.368,-1.6) rot=(0.707107,-0.707107,0;3.14159rad)
FEATURE [Part::Feature] Shape012  label="U3_LQFP_64_10x10mm_P05mm_ad08613fb525"
  Placement = pos=(36.576,-34.101,-1.6) rot=(1,0,0;3.14159rad)
  shape: bbox 12 x 12 x 1.5 mm, 1004 faces (baked)
FEATURE [App::Link] R42_R_0603_1608Metric_e00ced120b5b_ln_043  label="R45_R_0603_1608Metric_73e532b6d87c"
  LinkPlacement = pos=(69.469,-20.066,-1.6) rot=(0,1,0;3.14159rad)
  LinkedObject = -> Shape002
  Placement = pos=(69.469,-20.066,-1.6) rot=(0,1,0;3.14159rad)
FEATURE [App::Link] C18_C_0603_1608Metric_10e447ca614a_ln_016  label="C24_C_0603_1608Metric_f180910c596f"
  LinkPlacement = pos=(50.292,-32.893,-1.6) rot=(0.707107,-0.707107,0;3.14159rad)
  LinkedObject = -> Shape001
  Placement = pos=(50.292,-32.893,-1.6) rot=(0.707107,-0.707107,0;3.14159rad)
FEATURE [App::Link] R42_R_0603_1608Metric_e00ced120b5b_ln_044  label="R22_R_0603_1608Metric_74d0720be528"
  LinkPlacement = pos=(51.181,-35.433,-1.6) rot=(0,1,0;3.14159rad)
  LinkedObject = -> Shape002
  Placement = pos=(51.181,-35.433,-1.6) rot=(0,1,0;3.14159rad)
FEATURE [App::Link] R42_R_0603_1608Metric_e00ced120b5b_ln_045  label="R47_R_0603_1608Metric_036ee63e5562"
  LinkPlacement = pos=(55.88,-17.399,-1.6) rot=(0,1,0;3.14159rad)
  LinkedObject = -> Shape002
  Placement = pos=(55.88,-17.399,-1.6) rot=(0,1,0;3.14159rad)
FEATURE [App::Link] C21_CP_Radial_D80mm_P350mm_b4bb79b80bd8_ln_  label="C13_CP_Radial_D80mm_P350mm_7da63d23e92e"
  LinkPlacement = pos=(65.222,-55.753,-1.6) rot=(0,1,0;3.14159rad)
  LinkedObject = -> Shape003
  Placement = pos=(65.222,-55.753,-1.6) rot=(0,1,0;3.14159rad)
FEATURE [App::Part] Bot_e9e
  Group = -> [Shape,Shape001,Shape002,R42_R_0603_1608Metric_e00ced120b5b_ln_,R42_R_0603_1608Metric_e00ced120b5b_ln_001,Shape003,C19_C_0805_2012Metric_915db11c73f1_ln_,Shape004,R42_R_0603_1608Metric_e00ced120b5b_ln_002,C18_C_0603_1608Metric_10e447ca614a_ln_,R42_R_0603_1608Metric_e00ced120b5b_ln_003,R42_R_0603_1608Metric_e00ced120b5b_ln_004,Shape005,U2_SOT_23_5143090a7d01_ln_,+97 more]
  Origin = -> Origin004
FEATURE [App::Part] Step_Models_e9e
  Group = -> [Bot_e9e]
  Origin = -> Origin002
FEATURE [Part::Feature] pads_area001  label="topPads_e9e"
  Placement = pos=(0,0,0.02) rot=(0,0,1;0rad)
  shape: bbox 64.55 x 49.94 x 2e-07 mm, 250 faces, 0 solids (baked)
FEATURE [Part::Feature] Shape014  label="topTracks_e9e"
  Placement = pos=(0,0,0.01) rot=(0,0,1;0rad)
  shape: bbox 61.73 x 46.61 x 6.02e-05 mm, 42 faces, 0 solids (baked)
FEATURE [Part::Feature] zones_area001  label="topZones_e9e"
  Placement = pos=(0,0,0.01) rot=(0,0,1;0rad)
  shape: bbox 66.12 x 49.03 x 2e-07 mm, 6 faces, 0 solids (baked)
FEATURE [Part::Feature] pads_area003  label="botPads_e9e"
  Placement = pos=(0,0,-1.62) rot=(0,0,1;0rad)
  shape: bbox 64.55 x 49.94 x 2e-07 mm, 555 faces, 0 solids (baked)
FEATURE [Part::Feature] Shape016  label="botTracks_e9e"
  Placement = pos=(0,0,-1.61) rot=(0,0,1;0rad)
  shape: bbox 64.42 x 52.19 x 6.02e-05 mm, 194 faces, 0 solids (baked)
FEATURE [App::Part] Board_Geoms_e9e
  Group = -> [Pcb_e9e,PCB_Sketch_e9e,pads_area001,Shape014,zones_area001,pads_area003,Shape016]
  Origin = -> Origin
FEATURE [App::Part] Board_e9e  label="DIC"
  Group = -> [Local_CS_e9e,Board_Geoms_e9e,Step_Models_e9e]
  Origin = -> Origin001
